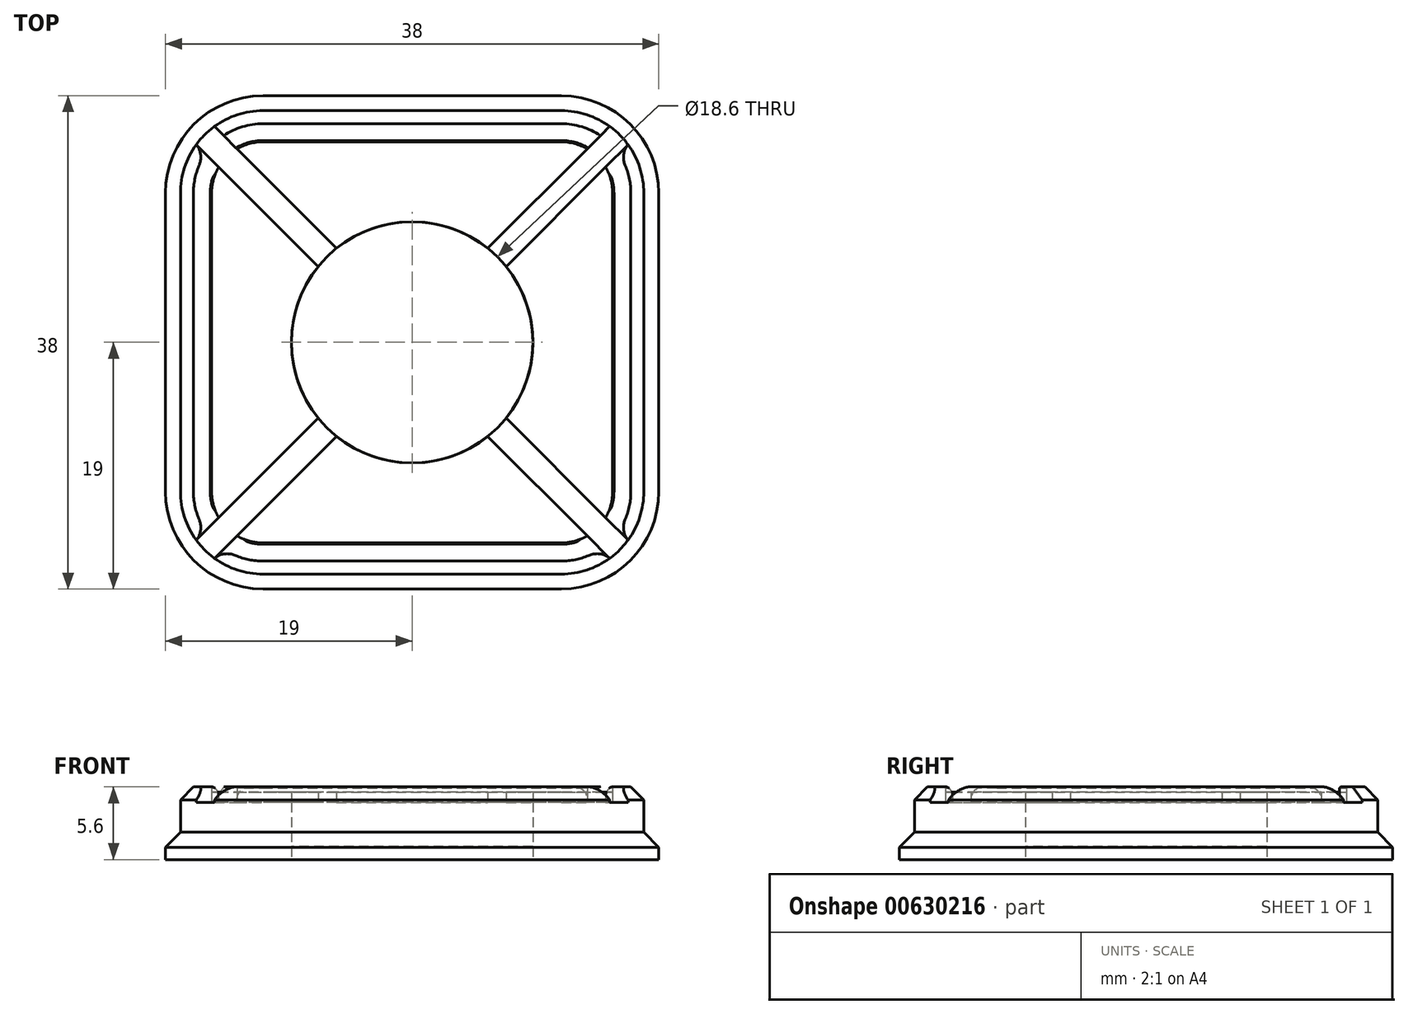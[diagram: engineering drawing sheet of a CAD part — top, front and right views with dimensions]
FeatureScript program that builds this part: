
annotation { "Feature Type Name" : "Feature", "Feature Type Description" : "" }
export const myFeature = defineFeature(function(context is Context, id is Id, definition is map)
    precondition{}
    {
        {
            var Q0;
            Q0=qCreatedBy(makeId("Top.planeOp"),FACE);
            var sketch = newSketch(context, id + "F0", { "sketchPlane" : qUnion([Q0])});
            skLineSegment(sketch, "E0.bottom", {"start": v(11.5, 19) * mm, "end": v(-11.5, 19) * mm});
            skLineSegment(sketch, "E0.top", {"start": v(11.5, -19) * mm, "end": v(-11.5, -19) * mm});
            skLineSegment(sketch, "E0.left", {"start": v(19, 11.5) * mm, "end": v(19, -11.5) * mm});
            skLineSegment(sketch, "E0.right", {"start": v(-19, 11.5) * mm, "end": v(-19, -11.5) * mm});
            skPoint(sketch, "E0.middle", {"position": v(0, 0) * mm});
            skPoint(sketch, "E1.visualSharp", {"position": v(-19, 19) * mm});
            skArc(sketch, "E1.filletArc", {"start": v(-11.5, 19) * mm, "mid": v(-16.8, 16.8) * mm, "end": v(-19, 11.5) * mm});
            skPoint(sketch, "E2.visualSharp", {"position": v(19, 19) * mm});
            skArc(sketch, "E2.filletArc", {"start": v(19, 11.5) * mm, "mid": v(16.8, 16.8) * mm, "end": v(11.5, 19) * mm});
            skPoint(sketch, "E3.visualSharp", {"position": v(19, -19) * mm});
            skArc(sketch, "E3.filletArc", {"start": v(11.5, -19) * mm, "mid": v(16.8, -16.8) * mm, "end": v(19, -11.5) * mm});
            skPoint(sketch, "E4.visualSharp", {"position": v(-19, -19) * mm});
            skArc(sketch, "E4.filletArc", {"start": v(-19, -11.5) * mm, "mid": v(-16.8, -16.8) * mm, "end": v(-11.5, -19) * mm});
            skArc(sketch, "E5.0", {"start": v(11.5, -17.85) * mm, "mid": v(16, -16) * mm, "end": v(17.85, -11.5) * mm});
            skLineSegment(sketch, "E5.1", {"start": v(17.85, 11.5) * mm, "end": v(17.85, -11.5) * mm});
            skLineSegment(sketch, "E5.2", {"start": v(11.5, -17.85) * mm, "end": v(-11.5, -17.85) * mm});
            skArc(sketch, "E5.3", {"start": v(17.85, 11.5) * mm, "mid": v(16, 16) * mm, "end": v(11.5, 17.85) * mm});
            skArc(sketch, "E5.4", {"start": v(-17.85, -11.5) * mm, "mid": v(-16, -16) * mm, "end": v(-11.5, -17.85) * mm});
            skLineSegment(sketch, "E5.5", {"start": v(-17.85, 11.5) * mm, "end": v(-17.85, -11.5) * mm});
            skArc(sketch, "E5.6", {"start": v(-11.5, 17.85) * mm, "mid": v(-16, 16) * mm, "end": v(-17.85, 11.5) * mm});
            skLineSegment(sketch, "E5.7", {"start": v(11.5, 17.85) * mm, "end": v(-11.5, 17.85) * mm});
            skArc(sketch, "E6.0", {"start": v(15.45, 11.5) * mm, "mid": v(14.3, 14.3) * mm, "end": v(11.5, 15.45) * mm});
            skLineSegment(sketch, "E6.1", {"start": v(15.45, 11.5) * mm, "end": v(15.45, -11.5) * mm});
            skLineSegment(sketch, "E6.2", {"start": v(11.5, 15.45) * mm, "end": v(-11.5, 15.45) * mm});
            skArc(sketch, "E6.3", {"start": v(11.5, -15.45) * mm, "mid": v(14.3, -14.3) * mm, "end": v(15.45, -11.5) * mm});
            skArc(sketch, "E6.4", {"start": v(-11.5, 15.45) * mm, "mid": v(-14.3, 14.3) * mm, "end": v(-15.45, 11.5) * mm});
            skLineSegment(sketch, "E6.5", {"start": v(-15.45, 11.5) * mm, "end": v(-15.45, -11.5) * mm});
            skArc(sketch, "E6.6", {"start": v(-15.45, -11.5) * mm, "mid": v(-14.3, -14.3) * mm, "end": v(-11.5, -15.45) * mm});
            skLineSegment(sketch, "E6.7", {"start": v(11.5, -15.45) * mm, "end": v(-11.5, -15.45) * mm});
            skCircle(sketch, "E7", {"center": v(0, 0) * mm, "radius": 9.3 * mm});
            skCircle(sketch, "E8", {"center": v(0, 0) * mm, "radius": 6.75 * mm, "construction": true});
            skSolve(sketch);
        }
        {
            var Q0;
            Q0=makeQuery(id+"F0.imprint","IMPRINT",FACE,{"disambiguationData":[TD([[makeQuery(id+"F0.imprint","IMPRINT",EDGE,{"derivedFrom":sQuery(id+"F0.wireOp",EDGE,"E0.bottom")}),1.0]])]});
            extrude(context, id + "F1", {"entities" : qUnion([Q0]), "depth" : (5.6 - 3.5) * mm, "offsetDistance" : 25 * mm});
        }
        {
            var Q0;
            Q0=makeQuery(id+"F0.imprint","IMPRINT",FACE,{"disambiguationData":[TD([[makeQuery(id+"F0.imprint","IMPRINT",EDGE,{"derivedFrom":sQuery(id+"F0.wireOp",EDGE,"E5.0")}),1.0]])]});
            extrude(context, id + "F2", {"entities" : qUnion([Q0]), "operationType" : NewBodyOperationType.ADD, "depth" : 5.6 * mm, "offsetDistance" : 25 * mm});
        }
        {
            var Q0;
            Q0=makeQuery(id+"F0.imprint","IMPRINT",FACE,{"disambiguationData":[TD([[makeQuery(id+"F0.imprint","IMPRINT",EDGE,{"derivedFrom":sQuery(id+"F0.wireOp",EDGE,"E6.0")}),1.0]])]});
            var Q1;
            Q1=makeQuery(id+"F2.opExtrude","CAP_FACE",FACE,{"disambiguationData":[OSD([sQuery(id+"F0.wireOp",EDGE,"E5.0"),sQuery(id+"F0.wireOp",EDGE,"E5.1"),sQuery(id+"F0.wireOp",EDGE,"E5.2"),sQuery(id+"F0.wireOp",EDGE,"E5.3"),sQuery(id+"F0.wireOp",EDGE,"E5.4"),sQuery(id+"F0.wireOp",EDGE,"E5.5"),sQuery(id+"F0.wireOp",EDGE,"E5.6"),sQuery(id+"F0.wireOp",EDGE,"E5.7"),sQuery(id+"F0.wireOp",EDGE,"E6.0"),sQuery(id+"F0.wireOp",EDGE,"E6.1"),sQuery(id+"F0.wireOp",EDGE,"E6.2"),sQuery(id+"F0.wireOp",EDGE,"E6.3"),sQuery(id+"F0.wireOp",EDGE,"E6.4"),sQuery(id+"F0.wireOp",EDGE,"E6.5"),sQuery(id+"F0.wireOp",EDGE,"E6.6"),sQuery(id+"F0.wireOp",EDGE,"E6.7")])],"isStart":false});
            extrude(context, id + "F3", {"entities" : qUnion([Q0]), "operationType" : NewBodyOperationType.ADD, "endBound" : BoundingType.UP_TO_SURFACE, "depth" : 5.2 * mm, "endBoundEntityFace" : qUnion([Q1]), "hasOffset" : true, "offsetDistance" : 1.2 * mm});
        }
        {
            var Q0;
            Q0=makeQuery(id+"F0.imprint","IMPRINT",FACE,{"disambiguationData":[TD([[makeQuery(id+"F0.imprint","IMPRINT",EDGE,{"derivedFrom":sQuery(id+"F0.wireOp",EDGE,"E7")}),1.0]])]});
            extrude(context, id + "F4", {"entities" : qUnion([Q0]), "depth" : 1 * mm, "offsetDistance" : 25 * mm});
        }
        {
            var Q0;
            Q0=makeQuery(id+"F1.opExtrude","CAP_EDGE",EDGE,{"disambiguationData":[OSD([sQuery(id+"F0.wireOp",EDGE,"E0.top")])],"isStart":false});
            chamfer(context, id + "F5", {"entities" : qUnion([Q0]), "width" : 1.15 * mm, "tangentPropagation" : true});
        }
        {
            var Q0;
            Q0=makeQuery(id+"F2.opExtrude","CAP_EDGE",EDGE,{"disambiguationData":[OSD([sQuery(id+"F0.wireOp",EDGE,"E5.2")])],"isStart":false});
            chamfer(context, id + "F6", {"entities" : qUnion([Q0]), "width" : 1 * mm, "tangentPropagation" : true});
        }
        {
            var Q0;
            Q0=makeQuery(id+"F2.opExtrude","CAP_EDGE",EDGE,{"disambiguationData":[OSD([sQuery(id+"F0.wireOp",EDGE,"E6.7")])],"isStart":false});
            chamfer(context, id + "F7", {"entities" : qUnion([Q0]), "width" : 0.1 * mm, "tangentPropagation" : true});
        }
        {
            var Q0;
            Q0=makeQuery(id+"F3.opExtrude","CAP_FACE",FACE,{"disambiguationData":[OSD([sQuery(id+"F0.wireOp",EDGE,"E5.0"),sQuery(id+"F0.wireOp",EDGE,"E5.1"),sQuery(id+"F0.wireOp",EDGE,"E5.2"),sQuery(id+"F0.wireOp",EDGE,"E5.3"),sQuery(id+"F0.wireOp",EDGE,"E5.4"),sQuery(id+"F0.wireOp",EDGE,"E5.5"),sQuery(id+"F0.wireOp",EDGE,"E5.6"),sQuery(id+"F0.wireOp",EDGE,"E5.7"),sQuery(id+"F0.wireOp",EDGE,"E6.0"),sQuery(id+"F0.wireOp",EDGE,"E6.1"),sQuery(id+"F0.wireOp",EDGE,"E6.2"),sQuery(id+"F0.wireOp",EDGE,"E6.3"),sQuery(id+"F0.wireOp",EDGE,"E6.4"),sQuery(id+"F0.wireOp",EDGE,"E6.5"),sQuery(id+"F0.wireOp",EDGE,"E6.6"),sQuery(id+"F0.wireOp",EDGE,"E6.7")])],"isStart":false});
            var Q1;
            Q1=makeQuery(id+"F3.opExtrude","CAP_FACE",FACE,{"disambiguationData":[OSD([sQuery(id+"F0.wireOp",EDGE,"E5.0"),sQuery(id+"F0.wireOp",EDGE,"E5.1"),sQuery(id+"F0.wireOp",EDGE,"E5.2"),sQuery(id+"F0.wireOp",EDGE,"E5.3"),sQuery(id+"F0.wireOp",EDGE,"E5.4"),sQuery(id+"F0.wireOp",EDGE,"E5.5"),sQuery(id+"F0.wireOp",EDGE,"E5.6"),sQuery(id+"F0.wireOp",EDGE,"E5.7"),sQuery(id+"F0.wireOp",EDGE,"E6.0"),sQuery(id+"F0.wireOp",EDGE,"E6.1"),sQuery(id+"F0.wireOp",EDGE,"E6.2"),sQuery(id+"F0.wireOp",EDGE,"E6.3"),sQuery(id+"F0.wireOp",EDGE,"E6.4"),sQuery(id+"F0.wireOp",EDGE,"E6.5"),sQuery(id+"F0.wireOp",EDGE,"E6.6"),sQuery(id+"F0.wireOp",EDGE,"E6.7")])],"isStart":false});
            extrude(context, id + "F8", {"entities" : qUnion([Q0]), "endBound" : BoundingType.UP_TO_SURFACE, "depth" : 25 * mm, "endBoundEntityFace" : qUnion([Q1]), "hasOffset" : true, "offsetDistance" : -0.8 * mm});
        }
        {
            var Q0;
            Q0=makeQuery(id+"F2.opExtrude","CAP_FACE",FACE,{"disambiguationData":[OSD([sQuery(id+"F0.wireOp",EDGE,"E5.0"),sQuery(id+"F0.wireOp",EDGE,"E5.1"),sQuery(id+"F0.wireOp",EDGE,"E5.2"),sQuery(id+"F0.wireOp",EDGE,"E5.3"),sQuery(id+"F0.wireOp",EDGE,"E5.4"),sQuery(id+"F0.wireOp",EDGE,"E5.5"),sQuery(id+"F0.wireOp",EDGE,"E5.6"),sQuery(id+"F0.wireOp",EDGE,"E5.7"),sQuery(id+"F0.wireOp",EDGE,"E6.0"),sQuery(id+"F0.wireOp",EDGE,"E6.1"),sQuery(id+"F0.wireOp",EDGE,"E6.2"),sQuery(id+"F0.wireOp",EDGE,"E6.3"),sQuery(id+"F0.wireOp",EDGE,"E6.4"),sQuery(id+"F0.wireOp",EDGE,"E6.5"),sQuery(id+"F0.wireOp",EDGE,"E6.6"),sQuery(id+"F0.wireOp",EDGE,"E6.7")])],"isStart":false});
            var sketch = newSketch(context, id + "F9", { "sketchPlane" : qUnion([Q0])});
            skLineSegment(sketch, "E9", {"start": v(-19, 17.59) * mm, "end": v(-0.7, -0.7) * mm});
            skLineSegment(sketch, "E10", {"start": v(-0.7, -0.7) * mm, "end": v(0.7, 0.7) * mm});
            skLineSegment(sketch, "E11", {"start": v(0.7, 0.7) * mm, "end": v(-17.59, 19) * mm});
            skLineSegment(sketch, "E12", {"start": v(-17.59, 19) * mm, "end": v(-19, 17.59) * mm});
            skPoint(sketch, "E13", {"position": v(0, 0) * mm});
            skLineSegment(sketch, "E14.1.0", {"start": v(-19, -17.59) * mm, "end": v(-17.59, -19) * mm});
            skLineSegment(sketch, "E14.1.1", {"start": v(-0.7, 0.7) * mm, "end": v(-19, -17.59) * mm});
            skLineSegment(sketch, "E14.1.3", {"start": v(-17.59, -19) * mm, "end": v(0.7, -0.7) * mm});
            skLineSegment(sketch, "E14.1.4", {"start": v(0.7, -0.7) * mm, "end": v(-0.7, 0.7) * mm});
            skLineSegment(sketch, "E14.2.0", {"start": v(17.59, -19) * mm, "end": v(19, -17.59) * mm});
            skLineSegment(sketch, "E14.2.1", {"start": v(-0.7, -0.7) * mm, "end": v(17.59, -19) * mm});
            skLineSegment(sketch, "E14.2.3", {"start": v(19, -17.59) * mm, "end": v(0.7, 0.7) * mm});
            skLineSegment(sketch, "E14.2.4", {"start": v(0.7, 0.7) * mm, "end": v(-0.7, -0.7) * mm});
            skLineSegment(sketch, "E14.3.0", {"start": v(19, 17.59) * mm, "end": v(17.59, 19) * mm});
            skLineSegment(sketch, "E14.3.1", {"start": v(0.7, -0.7) * mm, "end": v(19, 17.59) * mm});
            skLineSegment(sketch, "E14.3.3", {"start": v(17.59, 19) * mm, "end": v(-0.7, 0.7) * mm});
            skLineSegment(sketch, "E14.3.4", {"start": v(-0.7, 0.7) * mm, "end": v(0.7, -0.7) * mm});
            skSolve(sketch);
        }
        {
            var Q0;
            Q0 = qSketchRegion(id + "F9", true);
            var Q1;
            Q1=makeQuery(id+"F3.opExtrude","CAP_FACE",FACE,{"disambiguationData":[OSD([sQuery(id+"F0.wireOp",EDGE,"E5.0"),sQuery(id+"F0.wireOp",EDGE,"E5.1"),sQuery(id+"F0.wireOp",EDGE,"E5.2"),sQuery(id+"F0.wireOp",EDGE,"E5.3"),sQuery(id+"F0.wireOp",EDGE,"E5.4"),sQuery(id+"F0.wireOp",EDGE,"E5.5"),sQuery(id+"F0.wireOp",EDGE,"E5.6"),sQuery(id+"F0.wireOp",EDGE,"E5.7"),sQuery(id+"F0.wireOp",EDGE,"E6.0"),sQuery(id+"F0.wireOp",EDGE,"E6.1"),sQuery(id+"F0.wireOp",EDGE,"E6.2"),sQuery(id+"F0.wireOp",EDGE,"E6.3"),sQuery(id+"F0.wireOp",EDGE,"E6.4"),sQuery(id+"F0.wireOp",EDGE,"E6.5"),sQuery(id+"F0.wireOp",EDGE,"E6.6"),sQuery(id+"F0.wireOp",EDGE,"E6.7")])],"isStart":false});
            extrude(context, id + "F10", {"entities" : qUnion([Q0]), "operationType" : NewBodyOperationType.REMOVE, "endBound" : BoundingType.UP_TO_SURFACE, "oppositeDirection" : true, "depth" : 25 * mm, "endBoundEntityFace" : qUnion([Q1]), "offsetDistance" : 25 * mm});
        }
        {
            var Q0;
            Q0=makeQuery(id+"F10.boolean.opBoolean","COPY",EDGE,{"derivedFrom":makeQuery(id+"F10.opExtrude","CAP_EDGE",EDGE,{"disambiguationData":[OSD([sQuery(id+"F9.wireOp",EDGE,"E14.1.1")])],"isStart":true})});
            var Q1;
            Q1=makeQuery(id+"F10.boolean.opBoolean","COPY",EDGE,{"derivedFrom":makeQuery(id+"F10.opExtrude","CAP_EDGE",EDGE,{"disambiguationData":[OSD([sQuery(id+"F9.wireOp",EDGE,"E14.1.3")])],"isStart":true})});
            var Q2;
            Q2=makeQuery(id+"F10.boolean.opBoolean","COPY",EDGE,{"derivedFrom":makeQuery(id+"F10.opExtrude","CAP_EDGE",EDGE,{"disambiguationData":[OSD([sQuery(id+"F9.wireOp",EDGE,"E11")])],"isStart":true})});
            var Q3;
            Q3=makeQuery(id+"F10.boolean.opBoolean","COPY",EDGE,{"derivedFrom":makeQuery(id+"F10.opExtrude","CAP_EDGE",EDGE,{"disambiguationData":[OSD([sQuery(id+"F9.wireOp",EDGE,"E9")])],"isStart":true})});
            var Q4;
            Q4=makeQuery(id+"F10.boolean.opBoolean","COPY",EDGE,{"derivedFrom":makeQuery(id+"F10.opExtrude","CAP_EDGE",EDGE,{"disambiguationData":[OSD([sQuery(id+"F9.wireOp",EDGE,"E14.3.3")])],"isStart":true})});
            var Q5;
            Q5=makeQuery(id+"F10.boolean.opBoolean","COPY",EDGE,{"derivedFrom":makeQuery(id+"F10.opExtrude","CAP_EDGE",EDGE,{"disambiguationData":[OSD([sQuery(id+"F9.wireOp",EDGE,"E14.3.1")])],"isStart":true})});
            var Q6;
            Q6=makeQuery(id+"F10.boolean.opBoolean","COPY",EDGE,{"derivedFrom":makeQuery(id+"F10.opExtrude","CAP_EDGE",EDGE,{"disambiguationData":[OSD([sQuery(id+"F9.wireOp",EDGE,"E14.2.3")])],"isStart":true})});
            var Q7;
            Q7=makeQuery(id+"F10.boolean.opBoolean","COPY",EDGE,{"derivedFrom":makeQuery(id+"F10.opExtrude","CAP_EDGE",EDGE,{"disambiguationData":[OSD([sQuery(id+"F9.wireOp",EDGE,"E14.2.1")])],"isStart":true})});
            fillet(context, id + "F11", {"entities" : qUnion([Q0, Q1, Q2, Q3, Q4, Q5, Q6, Q7]), "radius" : 1 * mm, "tangentPropagation" : true, "allowEdgeOverflow" : false});
        }
        {
            var Q0;
            Q0=qCreatedBy(makeId("Top.planeOp"),FACE);
            cPlane(context, id + "F12", {"entities" : qUnion([Q0]), "cplaneType" : CPlaneType.OFFSET, "offset" : 11.2 * mm, "oppositeDirection" : true, "width" : 150 * mm, "height" : 150 * mm});
        }
        {
            var Q0;
            Q0=qCreatedBy(id+"F12.planeOp",FACE);
            var sketch = newSketch(context, id + "F13", { "sketchPlane" : qUnion([Q0])});
            skArc(sketch, "E15", {"start": v(0, 14) * mm, "mid": v(-14, 0) * mm, "end": v(0, -14) * mm});
            skLineSegment(sketch, "E16", {"start": v(0, 14) * mm, "end": v(0, -14) * mm});
            skSolve(sketch);
        }
        {
            var Q0;
            Q0=makeQuery(id+"F13.imprint","IMPRINT",FACE,{"disambiguationData":[TD([[makeQuery(id+"F13.imprint","IMPRINT",EDGE,{"derivedFrom":sQuery(id+"F13.wireOp",EDGE,"E15")}),1.0]])]});
            var Q1;
            Q1=sQuery(id+"F13.wireOp",EDGE,"E16");
            revolve(context, id + "F14", {"entities" : qUnion([Q0]), "axis" : qUnion([Q1]), "revolveType" : RevolveType.ONE_DIRECTION, "oppositeDirection" : true, "angle" : 180 * degree});
        }
        {
            var Q0;
            Q0=makeQuery(id+"F4.opExtrude","SWEPT_BODY",BODY,{"disambiguationData":[OSD([sQuery(id+"F0.wireOp",EDGE,"E7")])]});
            var Q1;
            Q1=makeQuery(id+"F14.opRevolve","SWEPT_BODY",BODY,{"disambiguationData":[OSD([sQuery(id+"F13.wireOp",EDGE,"E15"),sQuery(id+"F13.wireOp",EDGE,"E16")])]});
            booleanBodies(context, id + "F15", {"operationType" : BooleanOperationType.SUBTRACTION, "tools" : qUnion([Q0]), "targets" : qUnion([Q1]), "keepTools" : true});
        }
        {
            var Q0;
            Q0=makeQuery(id+"F15.opBoolean","SPLIT",BODY,{"disambiguationData":[OD(0.0)],"derivedFrom":makeQuery(id+"F14.opRevolve","SWEPT_BODY",BODY,{"disambiguationData":[OSD([sQuery(id+"F13.wireOp",EDGE,"E15"),sQuery(id+"F13.wireOp",EDGE,"E16")])]})});
            deleteBodies(context, id + "F16", {"entities" : qUnion([Q0])});
        }
        {
            var Q0;
            Q0=makeQuery(id+"F0.imprint","IMPRINT",FACE,{"disambiguationData":[TD([[makeQuery(id+"F0.imprint","IMPRINT",EDGE,{"derivedFrom":sQuery(id+"F0.wireOp",EDGE,"E7")}),1.0]])]});
            var Q1;
            Q1=makeQuery(id+"F8.opExtrude","CAP_FACE",FACE,{"disambiguationData":[OSD([sQuery(id+"F0.wireOp",EDGE,"E5.0"),sQuery(id+"F0.wireOp",EDGE,"E5.1"),sQuery(id+"F0.wireOp",EDGE,"E5.2"),sQuery(id+"F0.wireOp",EDGE,"E5.3"),sQuery(id+"F0.wireOp",EDGE,"E5.4"),sQuery(id+"F0.wireOp",EDGE,"E5.5"),sQuery(id+"F0.wireOp",EDGE,"E5.6"),sQuery(id+"F0.wireOp",EDGE,"E5.7"),sQuery(id+"F0.wireOp",EDGE,"E6.0"),sQuery(id+"F0.wireOp",EDGE,"E6.1"),sQuery(id+"F0.wireOp",EDGE,"E6.2"),sQuery(id+"F0.wireOp",EDGE,"E6.3"),sQuery(id+"F0.wireOp",EDGE,"E6.4"),sQuery(id+"F0.wireOp",EDGE,"E6.5"),sQuery(id+"F0.wireOp",EDGE,"E6.6"),sQuery(id+"F0.wireOp",EDGE,"E6.7")])],"isStart":false});
            var Q2;
            Q2=makeQuery(id+"F8.opExtrude","CAP_FACE",FACE,{"disambiguationData":[OSD([sQuery(id+"F0.wireOp",EDGE,"E5.0"),sQuery(id+"F0.wireOp",EDGE,"E5.1"),sQuery(id+"F0.wireOp",EDGE,"E5.2"),sQuery(id+"F0.wireOp",EDGE,"E5.3"),sQuery(id+"F0.wireOp",EDGE,"E5.4"),sQuery(id+"F0.wireOp",EDGE,"E5.5"),sQuery(id+"F0.wireOp",EDGE,"E5.6"),sQuery(id+"F0.wireOp",EDGE,"E5.7"),sQuery(id+"F0.wireOp",EDGE,"E6.0"),sQuery(id+"F0.wireOp",EDGE,"E6.1"),sQuery(id+"F0.wireOp",EDGE,"E6.2"),sQuery(id+"F0.wireOp",EDGE,"E6.3"),sQuery(id+"F0.wireOp",EDGE,"E6.4"),sQuery(id+"F0.wireOp",EDGE,"E6.5"),sQuery(id+"F0.wireOp",EDGE,"E6.6"),sQuery(id+"F0.wireOp",EDGE,"E6.7")])],"isStart":true});
            extrude(context, id + "F17", {"entities" : qUnion([Q0]), "endBound" : BoundingType.UP_TO_SURFACE, "depth" : 16.1 * mm, "endBoundEntityFace" : qUnion([Q1]), "offsetDistance" : 25 * mm, "hasSecondDirection" : true, "secondDirectionBound" : SecondDirectionBoundingType.UP_TO_SURFACE, "secondDirectionOppositeDirection" : false, "secondDirectionDepth" : 7.5 * mm, "secondDirectionBoundEntityFace" : qUnion([Q2])});
        }
    });
